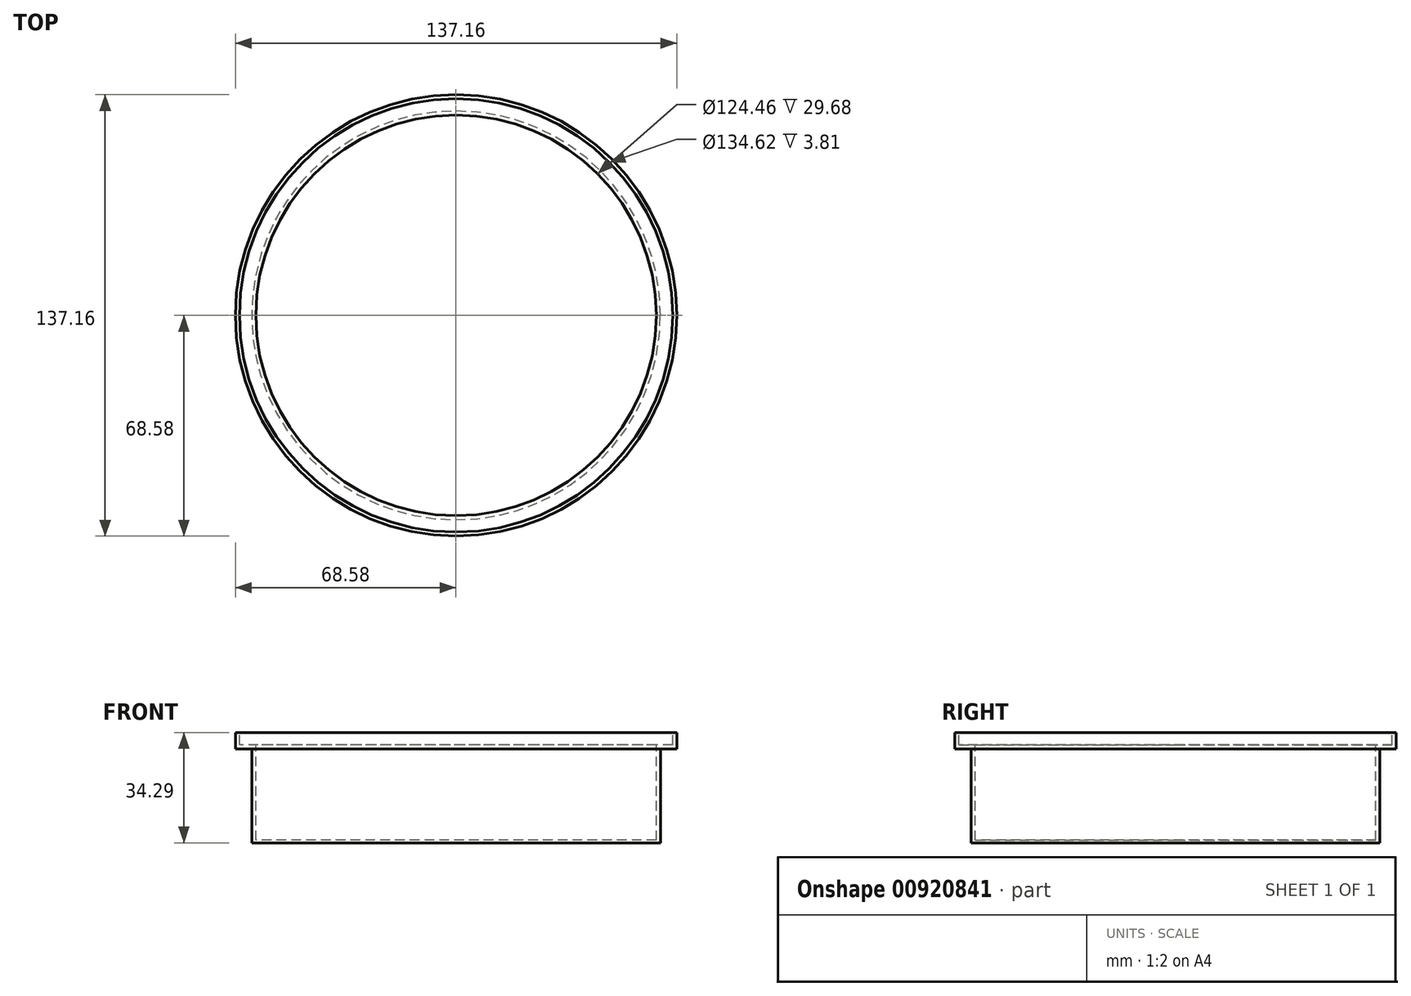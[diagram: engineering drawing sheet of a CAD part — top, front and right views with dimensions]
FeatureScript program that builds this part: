
annotation { "Feature Type Name" : "Feature", "Feature Type Description" : "" }
export const myFeature = defineFeature(function(context is Context, id is Id, definition is map)
    precondition{}
    {
        {
            var Q0;
            Q0=qCreatedBy(makeId("Front.planeOp"),FACE);
            var sketch = newSketch(context, id + "F0", { "sketchPlane" : qUnion([Q0])});
            skLineSegment(sketch, "E0", {"start": v(0, 0) * mm, "end": v(63.5, 0) * mm});
            skLineSegment(sketch, "E1", {"start": v(63.5, 0) * mm, "end": v(63.5, 29.21) * mm});
            skLineSegment(sketch, "E2", {"start": v(63.5, 29.21) * mm, "end": v(68.58, 29.21) * mm});
            skLineSegment(sketch, "E3", {"start": v(68.58, 29.21) * mm, "end": v(68.58, 34.3) * mm});
            skLineSegment(sketch, "E4", {"start": v(68.58, 34.3) * mm, "end": v(0, 34.3) * mm});
            skLineSegment(sketch, "E5", {"start": v(0, 34.3) * mm, "end": v(0, 0) * mm});
            skLineSegment(sketch, "E6", {"start": v(0, 0) * mm, "end": v(0, -28.54) * mm, "construction": true});
            skSolve(sketch);
        }
        {
            var Q0;
            Q0 = qSketchRegion(id + "F0", true);
            var Q1;
            Q1=sQuery(id+"F0.wireOp",EDGE,"E6");
            revolve(context, id + "F1", {"surfaceOperationType" : NewSurfaceOperationType.NEW, "entities" : qUnion([Q0]), "axis" : qUnion([Q1]), "revolveType" : RevolveType.FULL});
        }
        {
            var Q0;
            Q0=makeQuery(id+"F1.opRevolve","SWEPT_FACE",FACE,{"disambiguationData":[OSD([sQuery(id+"F0.wireOp",EDGE,"E4")])]});
            shell(context, id + "F2", {"entities" : qUnion([Q0]), "thickness" : 1.27 * mm});
        }
        {
            var Q0;
            Q0=makeQuery(id+"F2.opShell","OFFSET_FACE",FACE,{"disambiguationData":[OSD([sQuery(id+"F0.wireOp",EDGE,"E0")])]});
            var sketch = newSketch(context, id + "F3", { "sketchPlane" : qUnion([Q0])});
            skCircle(sketch, "E7", {"center": v(0, 0) * mm, "radius": 62.23 * mm});
            skSolve(sketch);
        }
        {
            var Q0;
            Q0 = qSketchRegion(id + "F3", true);
            var Q1;
            Q1=makeQuery(id+"F1.opRevolve","SWEPT_FACE",FACE,{"disambiguationData":[OSD([sQuery(id+"F0.wireOp",EDGE,"E0")])]});
            extrude(context, id + "F4", {"entities" : qUnion([Q0]), "operationType" : NewBodyOperationType.REMOVE, "endBound" : BoundingType.UP_TO_SURFACE, "oppositeDirection" : true, "depth" : 25.4 * mm, "endBoundEntityFace" : qUnion([Q1]), "hasOffset" : true, "offsetDistance" : .8 * mm});
        }
    });
